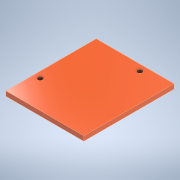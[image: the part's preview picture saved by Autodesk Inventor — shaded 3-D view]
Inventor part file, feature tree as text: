
AUTODESK INVENTOR PART (.ipt)
format: ipt  version: 2021 (Build 250183000, 183)  size: 103,936 bytes
history: native  units: mm
features: sketch x1, extrude x1, hole x1
ambient origin geometry x8: Origin, YZ Plane, XZ Plane, XY Plane, X Axis, Y Axis, Z Axis, Center Point
bodies: Solid1 (feature_tree)
feature tree (3):
  sketch  "Sketch1"  dims[d0=50.0mm d1=58.0mm d2=4.0mm d3=4.0mm d4=18.0mm d5=18.0mm d6=3.0mm d7=0.0mm d8=3.2mm d9=6.0mm d10=4.0mm d11=2.0mm d12=90.0deg d13=8.0mm d14=20.594885mm]
  extrude  "Extrusion1"  Depth=58.0mm
  hole  "Hole1"  [1 undecoded]
note: 1 required parameter value undecoded (feature->parameter linkage not recoverable at this tier; creation-order binding heuristic only, values carry confidence <= 0.55)
